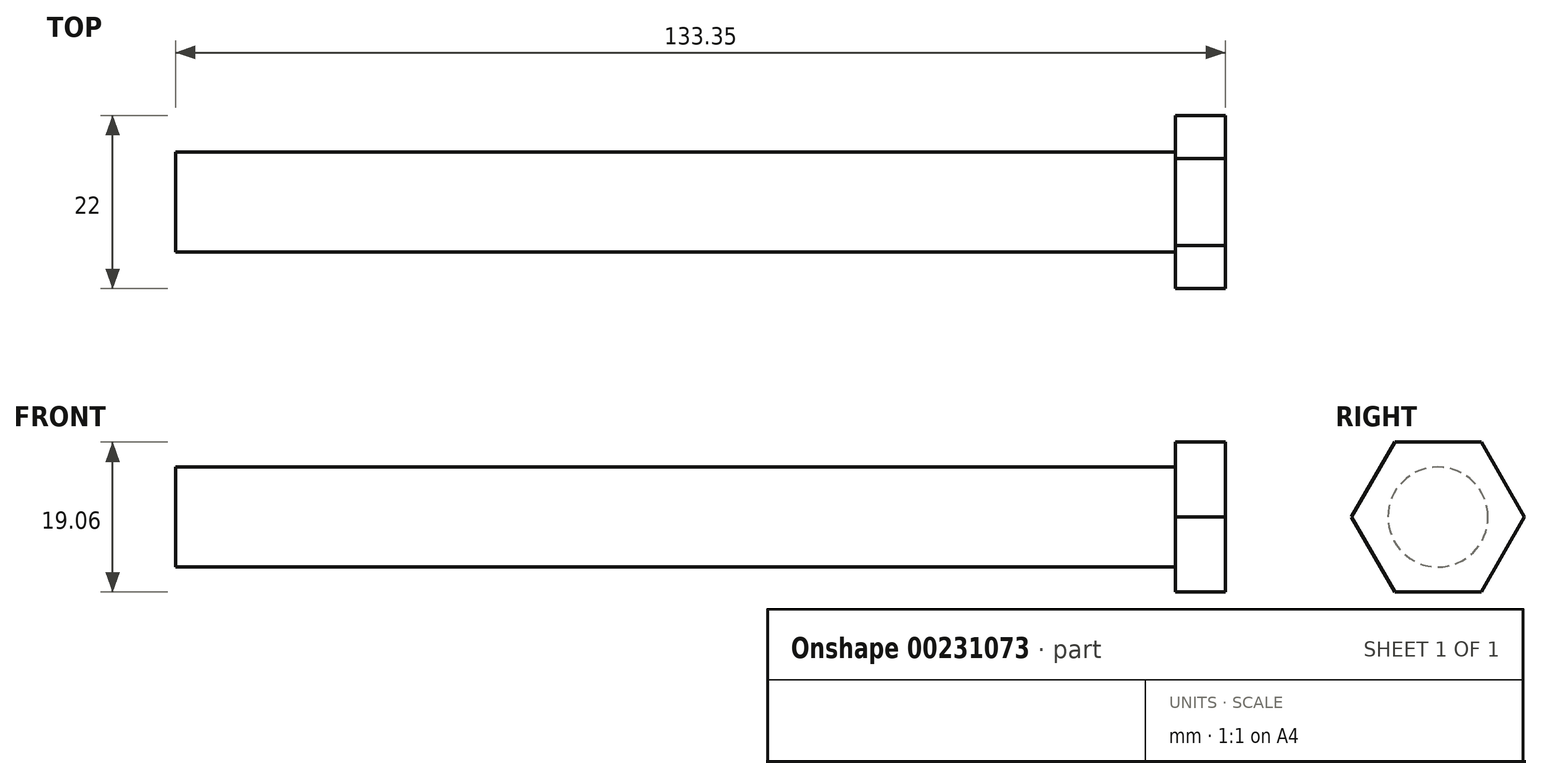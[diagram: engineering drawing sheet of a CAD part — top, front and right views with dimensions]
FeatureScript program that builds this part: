
annotation { "Feature Type Name" : "Feature", "Feature Type Description" : "" }
export const myFeature = defineFeature(function(context is Context, id is Id, definition is map)
    precondition{}
    {
        {
            var Q0;
            Q0=qCreatedBy(makeId("Right.planeOp"),FACE);
            var sketch = newSketch(context, id + "F0", { "sketchPlane" : qUnion([Q0])});
            skCircle(sketch, "E0", {"center": v(0, 0) * mm, "radius": 6.35 * mm});
            skSolve(sketch);
        }
        {
            var Q0;
            Q0=qSketchRegion(id+"F0",true);
            extrude(context, id + "F1", {"entities" : qUnion([Q0]), "depth" : 127 * mm});
        }
        {
            var Q0;
            Q0=makeQuery(id+"F1.opExtrude","CAP_FACE",FACE,{"disambiguationData":[OSD([sQuery(id+"F0.wireOp",EDGE,"E0")])],"isStart":false});
            var sketch = newSketch(context, id + "F2", { "sketchPlane" : qUnion([Q0])});
            skCircle(sketch, "E1.cCircle", {"center": v(0, 0) * mm, "radius": 9.53 * mm, "construction": true});
            skLineSegment(sketch, "E1.0", {"start": v(-5.5, 9.53) * mm, "end": v(5.5, 9.53) * mm});
            skLineSegment(sketch, "E1.1", {"start": v(5.5, 9.53) * mm, "end": v(11, 0) * mm});
            skLineSegment(sketch, "E1.2", {"start": v(11, 0) * mm, "end": v(5.5, -9.53) * mm});
            skLineSegment(sketch, "E1.3", {"start": v(5.5, -9.52) * mm, "end": v(-5.5, -9.53) * mm});
            skLineSegment(sketch, "E1.4", {"start": v(-5.5, -9.53) * mm, "end": v(-11, 0) * mm});
            skLineSegment(sketch, "E1.5", {"start": v(-11, 0) * mm, "end": v(-5.5, 9.52) * mm});
            skPoint(sketch, "E1.0.midPoint", {"position": v(0, 9.53) * mm});
            skSolve(sketch);
        }
        {
            var Q0;
            Q0=qSketchRegion(id+"F2",true);
            extrude(context, id + "F3", {"entities" : qUnion([Q0]), "operationType" : NewBodyOperationType.ADD, "depth" : 6.35 * mm});
        }
    });
